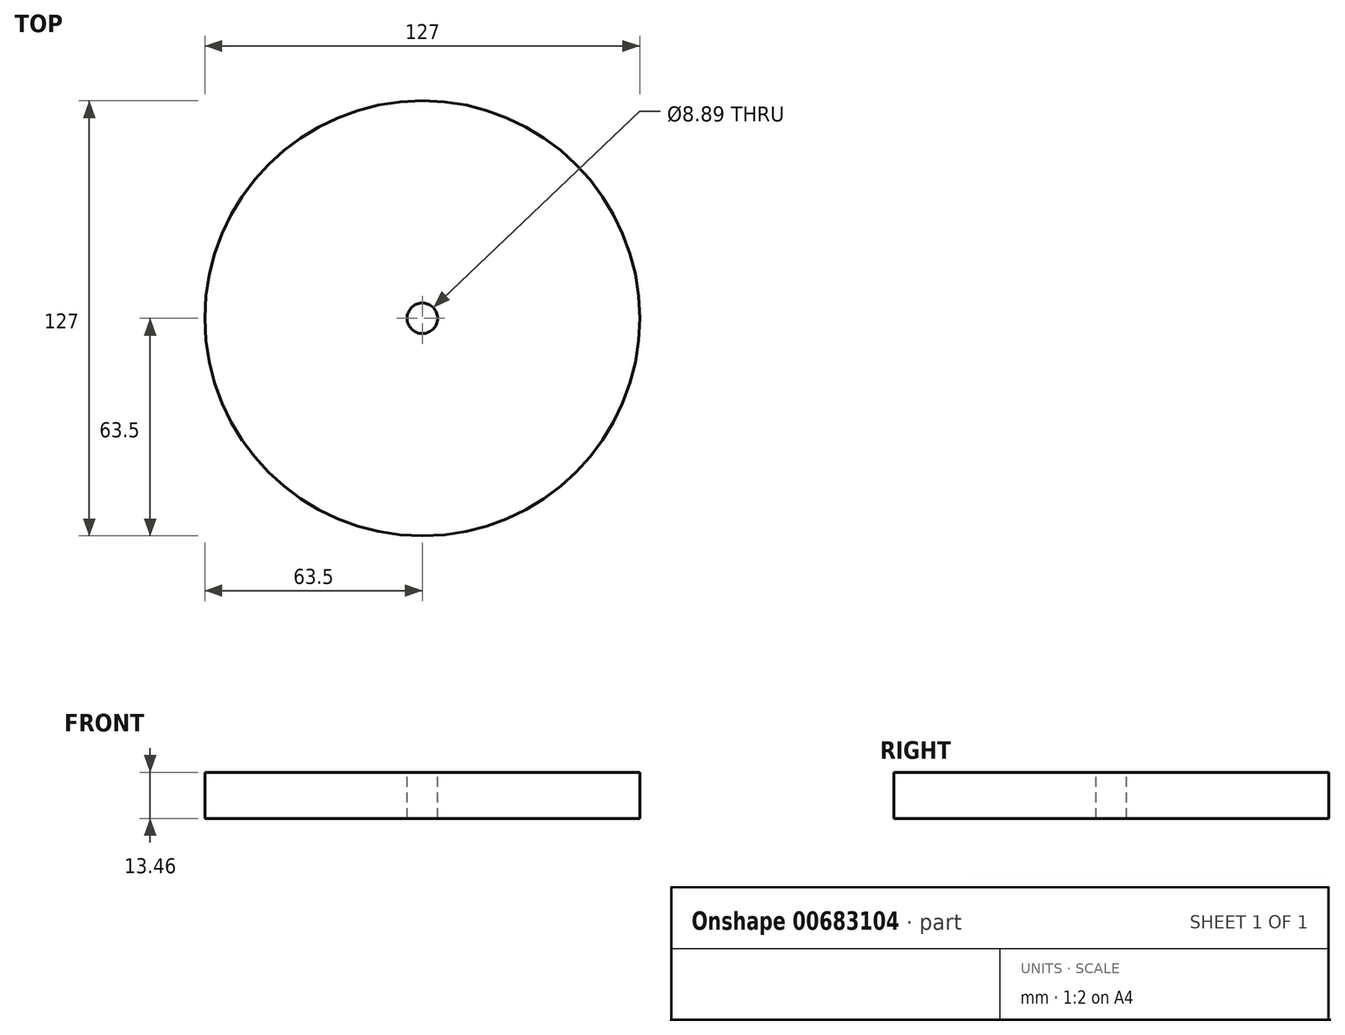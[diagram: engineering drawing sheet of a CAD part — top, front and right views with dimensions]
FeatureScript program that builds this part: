
annotation { "Feature Type Name" : "Feature", "Feature Type Description" : "" }
export const myFeature = defineFeature(function(context is Context, id is Id, definition is map)
    precondition{}
    {
        {
            var Q0;
            Q0=qCreatedBy(makeId("Top.planeOp"),FACE);
            var sketch = newSketch(context, id + "F0", { "sketchPlane" : qUnion([Q0])});
            skCircle(sketch, "E0", {"center": v(0, 0) * mm, "radius": 63.5 * mm});
            skLineSegment(sketch, "E1", {"start": v(0, 63.5) * mm, "end": v(0, -63.5) * mm});
            skLineSegment(sketch, "E2", {"start": v(-63.5, 0) * mm, "end": v(63.5, 0) * mm});
            skCircle(sketch, "E3", {"center": v(0, 0) * mm, "radius": 4.45 * mm});
            skSolve(sketch);
        }
        {
            var Q0;
            {var subQ0=sQuery(id+"F0.wireOp",EDGE,"E1");var subQ1=sQuery(id+"F0.wireOp",EDGE,"E0");var subQ2=makeQuery(id+"F0.imprint","INTERSECT",VERTEX,{"disambiguationData":[OD(1.0)],"derivedFrom":[subQ1,subQ0]});Q0=makeQuery(id+"F0.imprint","IMPRINT",FACE,{"disambiguationData":[TD([[makeQuery(id+"F0.imprint","IMPRINT",EDGE,{"disambiguationData":[TD([[subQ2,1.0]])],"derivedFrom":subQ1}),1.0]])]});}
            var Q1;
            {var subQ0=sQuery(id+"F0.wireOp",EDGE,"E1");var subQ1=sQuery(id+"F0.wireOp",EDGE,"E0");var subQ2=makeQuery(id+"F0.imprint","INTERSECT",VERTEX,{"disambiguationData":[OD(1.0)],"derivedFrom":[subQ1,subQ0]});Q1=makeQuery(id+"F0.imprint","IMPRINT",FACE,{"disambiguationData":[TD([[makeQuery(id+"F0.imprint","IMPRINT",EDGE,{"disambiguationData":[TD([[subQ2,-1.0]])],"derivedFrom":subQ1}),1.0]])]});}
            var Q2;
            {var subQ0=sQuery(id+"F0.wireOp",EDGE,"E1");var subQ1=sQuery(id+"F0.wireOp",EDGE,"E0");var subQ2=makeQuery(id+"F0.imprint","INTERSECT",VERTEX,{"disambiguationData":[OD(0.0)],"derivedFrom":[subQ1,subQ0]});Q2=makeQuery(id+"F0.imprint","IMPRINT",FACE,{"disambiguationData":[TD([[makeQuery(id+"F0.imprint","IMPRINT",EDGE,{"disambiguationData":[TD([[subQ2,-1.0]])],"derivedFrom":subQ1}),1.0]])]});}
            var Q3;
            {var subQ0=sQuery(id+"F0.wireOp",EDGE,"E1");var subQ1=sQuery(id+"F0.wireOp",EDGE,"E0");var subQ2=makeQuery(id+"F0.imprint","INTERSECT",VERTEX,{"disambiguationData":[OD(0.0)],"derivedFrom":[subQ1,subQ0]});Q3=makeQuery(id+"F0.imprint","IMPRINT",FACE,{"disambiguationData":[TD([[makeQuery(id+"F0.imprint","IMPRINT",EDGE,{"disambiguationData":[TD([[subQ2,1.0]])],"derivedFrom":subQ1}),1.0]])]});}
            extrude(context, id + "F1", {"entities" : qUnion([Q0, Q1, Q2, Q3]), "oppositeDirection" : true, "depth" : 13.46 * mm, "offsetDistance" : 25.4 * mm});
        }
    });
